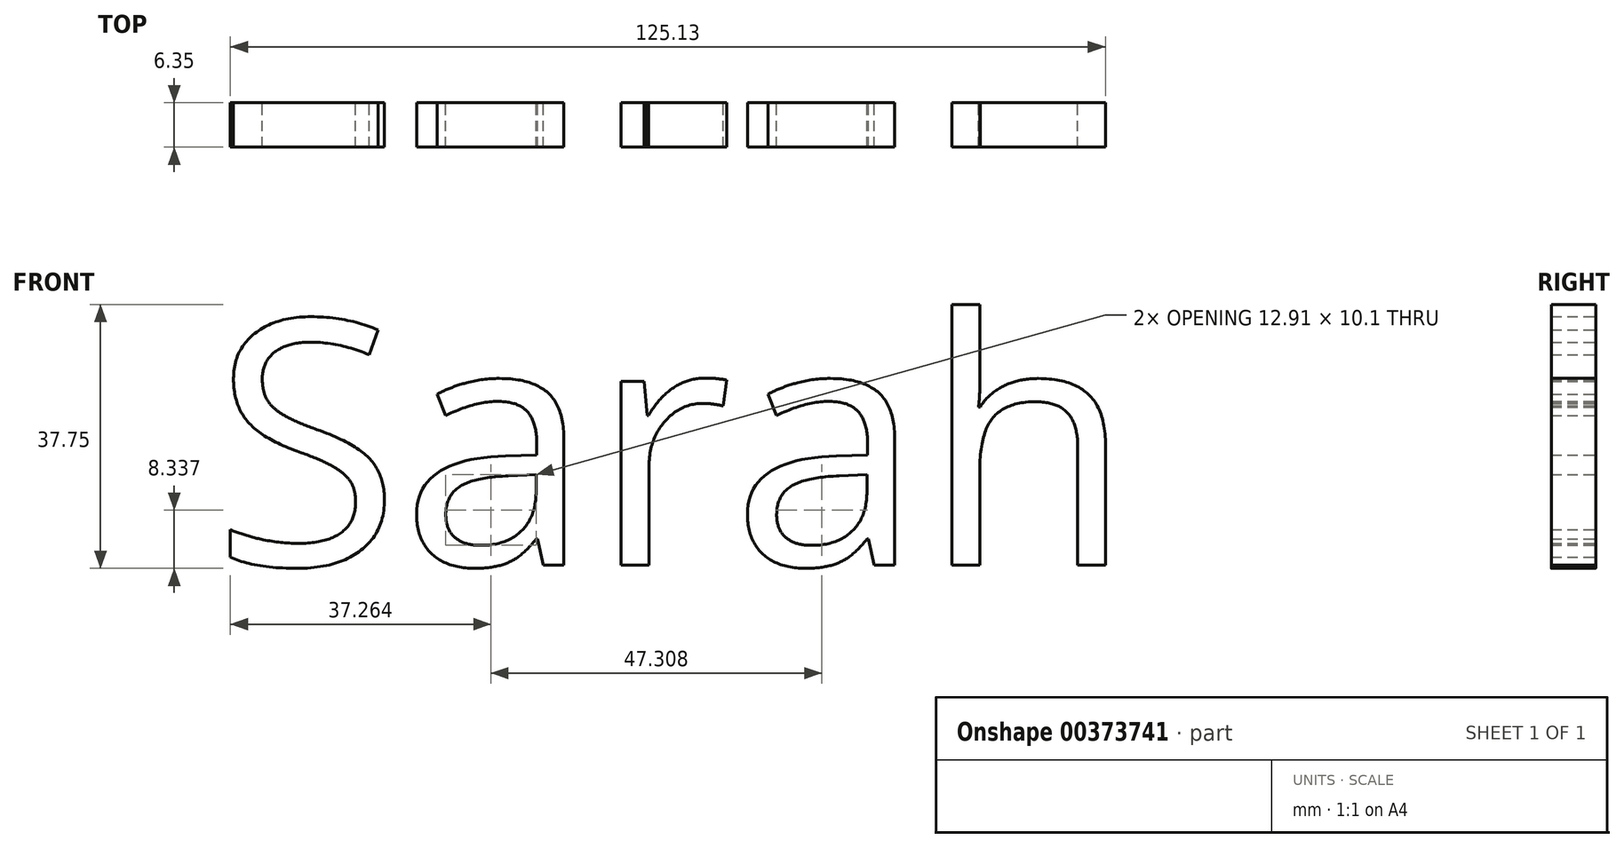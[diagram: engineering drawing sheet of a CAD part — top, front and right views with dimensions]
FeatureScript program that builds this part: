
annotation { "Feature Type Name" : "Feature", "Feature Type Description" : "" }
export const myFeature = defineFeature(function(context is Context, id is Id, definition is map)
    precondition{}
    {
        {
            var Q0;
            Q0=qCreatedBy(makeId("Front.planeOp"),FACE);
            var sketch = newSketch(context, id + "F0", { "sketchPlane" : qUnion([Q0])});
            skText(sketch, "E0", { "text": "Sarah", "fontName": "OpenSans-Regular.ttf"});
            const initialGuessF0  = {"E0": [-0.06902, -0.01668, 1, 0, 0.03532]};
            skSetInitialGuess(sketch, initialGuessF0);
            skSolve(sketch);
        }
        {
            var Q0;
            Q0 = qSketchRegion(id + "F0", true);
            extrude(context, id + "F1", {"entities" : qUnion([Q0]), "depth" : 6.35 * mm});
        }
    });
